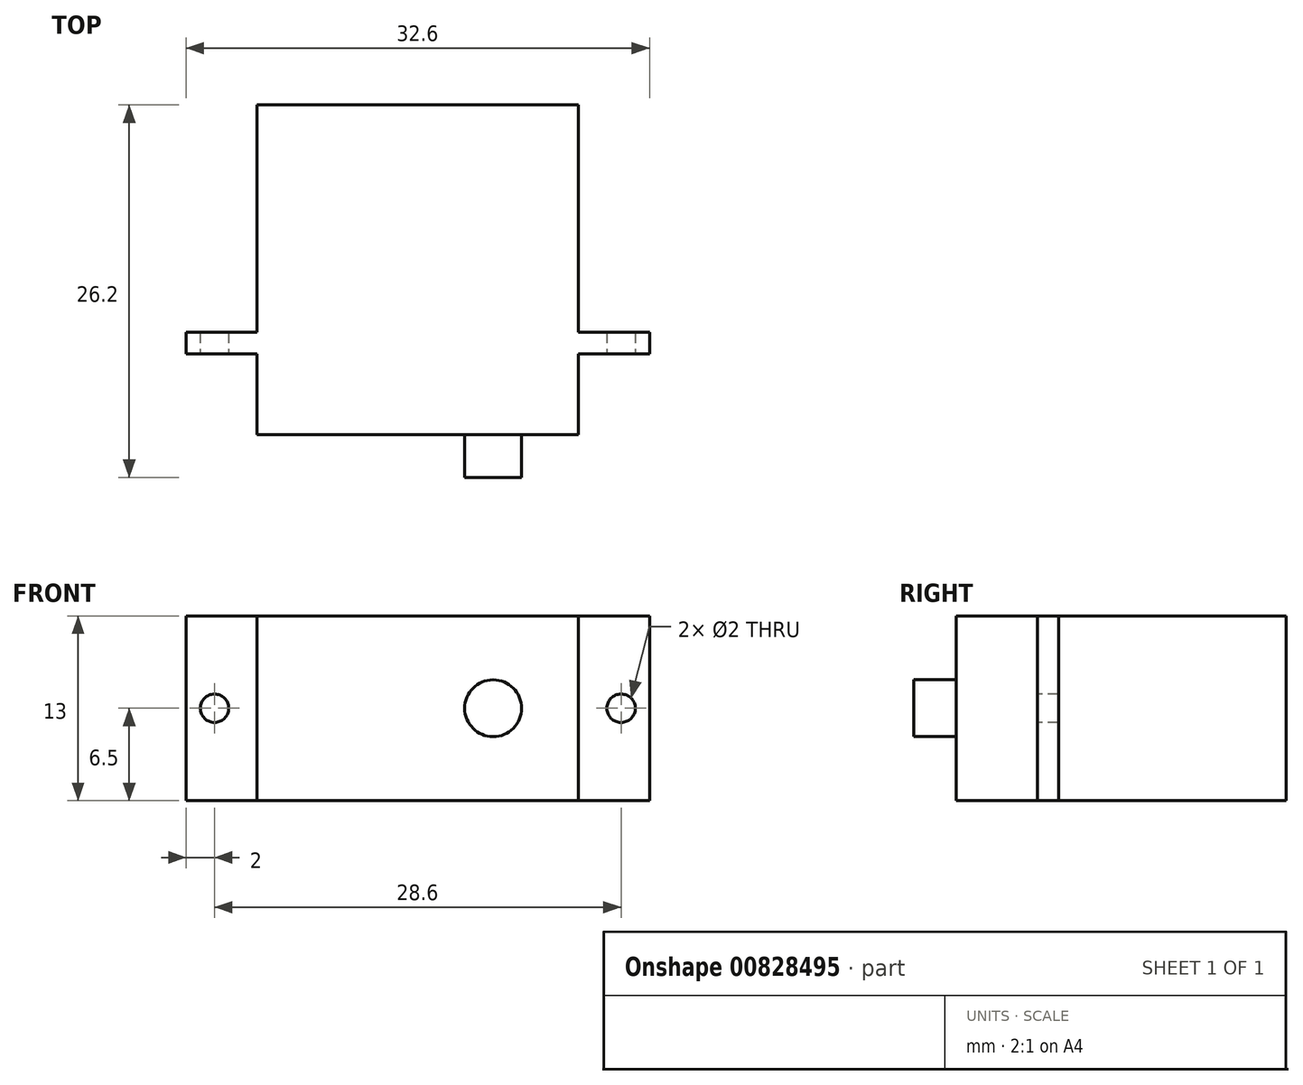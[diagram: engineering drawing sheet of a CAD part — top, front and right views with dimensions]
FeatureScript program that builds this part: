
annotation { "Feature Type Name" : "Feature", "Feature Type Description" : "" }
export const myFeature = defineFeature(function(context is Context, id is Id, definition is map)
    precondition{}
    {
        {
            var Q0;
            Q0=qCreatedBy(makeId("Top.planeOp"),FACE);
            var sketch = newSketch(context, id + "F0", { "sketchPlane" : qUnion([Q0])});
            skLineSegment(sketch, "E0", {"start": v(-33.3, 20.69) * mm, "end": v(-10.7, 20.69) * mm});
            skLineSegment(sketch, "E1", {"start": v(-10.7, 20.69) * mm, "end": v(-10.7, 4.69) * mm});
            skLineSegment(sketch, "E2", {"start": v(-10.7, 4.69) * mm, "end": v(-5.7, 4.69) * mm});
            skLineSegment(sketch, "E3", {"start": v(-5.7, 4.69) * mm, "end": v(-5.7, 3.19) * mm});
            skLineSegment(sketch, "E4", {"start": v(-5.7, 3.19) * mm, "end": v(-10.7, 3.19) * mm});
            skLineSegment(sketch, "E5", {"start": v(-10.7, 3.19) * mm, "end": v(-10.7, -2.51) * mm});
            skLineSegment(sketch, "E6", {"start": v(-10.7, -2.51) * mm, "end": v(-33.3, -2.51) * mm});
            skLineSegment(sketch, "E7", {"start": v(-33.3, -2.51) * mm, "end": v(-33.3, 3.19) * mm});
            skLineSegment(sketch, "E8", {"start": v(-33.3, 3.19) * mm, "end": v(-38.3, 3.19) * mm});
            skLineSegment(sketch, "E9", {"start": v(-38.3, 3.19) * mm, "end": v(-38.3, 4.69) * mm});
            skLineSegment(sketch, "E10", {"start": v(-38.3, 4.69) * mm, "end": v(-33.3, 4.69) * mm});
            skLineSegment(sketch, "E11", {"start": v(-33.3, 4.69) * mm, "end": v(-33.3, 20.69) * mm});
            skPoint(sketch, "E12", {"position": v(-16.7, -2.51) * mm});
            skPoint(sketch, "E13", {"position": v(-16.7, -8.17) * mm});
            skLineSegment(sketch, "E14", {"start": v(-16.7, -2.51) * mm, "end": v(-16.7, -8.17) * mm, "construction": true});
            skSolve(sketch);
        }
        {
            var Q0;
            Q0=makeQuery(id+"F0.imprint","IMPRINT",FACE,{"disambiguationData":[TD([[makeQuery(id+"F0.imprint","IMPRINT",EDGE,{"derivedFrom":sQuery(id+"F0.wireOp",EDGE,"E0")}),-1.0]])]});
            extrude(context, id + "F1", {"entities" : qUnion([Q0]), "depth" : 13 * mm, "offsetDistance" : 25 * mm});
        }
        {
            var Q0;
            Q0=makeQuery(id+"F1.opExtrude","SWEPT_FACE",FACE,{"disambiguationData":[OSD([sQuery(id+"F0.wireOp",EDGE,"E4")])]});
            var sketch = newSketch(context, id + "F2", { "sketchPlane" : qUnion([Q0])});
            skLineSegment(sketch, "E15.0.0", {"start": v(-38.3, 0) * mm, "end": v(-33.3, 0) * mm, "construction": true});
            skLineSegment(sketch, "E15.0.1", {"start": v(-33.3, 0) * mm, "end": v(-33.3, 13) * mm, "construction": true});
            skLineSegment(sketch, "E15.0.2", {"start": v(-33.3, 13) * mm, "end": v(-38.3, 13) * mm, "construction": true});
            skLineSegment(sketch, "E15.0.3", {"start": v(-38.3, 13) * mm, "end": v(-38.3, 0) * mm, "construction": true});
            skLineSegment(sketch, "E16.0", {"start": v(-5.7, 13) * mm, "end": v(-10.7, 13) * mm, "construction": true});
            skLineSegment(sketch, "E16.1", {"start": v(-5.7, 13) * mm, "end": v(-5.7, 0) * mm, "construction": true});
            skLineSegment(sketch, "E16.2", {"start": v(-10.7, 13) * mm, "end": v(-10.7, 0) * mm, "construction": true});
            skLineSegment(sketch, "E16.3", {"start": v(-5.7, 0) * mm, "end": v(-10.7, 0) * mm, "construction": true});
            skLineSegment(sketch, "E17", {"start": v(-5.7, 6.5) * mm, "end": v(-7.7, 6.5) * mm, "construction": true});
            skLineSegment(sketch, "E18", {"start": v(-38.3, 6.5) * mm, "end": v(-36.3, 6.5) * mm, "construction": true});
            skCircle(sketch, "E19", {"center": v(-36.3, 6.5) * mm, "radius": 1 * mm});
            skCircle(sketch, "E20", {"center": v(-7.7, 6.5) * mm, "radius": 1 * mm});
            skSolve(sketch);
        }
        {
            var Q0;
            Q0=makeQuery(id+"F2.imprint","IMPRINT",FACE,{"disambiguationData":[TD([[makeQuery(id+"F2.imprint","IMPRINT",EDGE,{"derivedFrom":sQuery(id+"F2.wireOp",EDGE,"E19")}),1.0]])]});
            var Q1;
            Q1=makeQuery(id+"F2.imprint","IMPRINT",FACE,{"disambiguationData":[TD([[makeQuery(id+"F2.imprint","IMPRINT",EDGE,{"derivedFrom":sQuery(id+"F2.wireOp",EDGE,"E20")}),1.0]])]});
            var Q2;
            Q2=makeQuery(id+"F1.opExtrude","SWEPT_FACE",FACE,{"disambiguationData":[OSD([sQuery(id+"F0.wireOp",EDGE,"E2")])]});
            extrude(context, id + "F3", {"entities" : qUnion([Q0, Q1]), "operationType" : NewBodyOperationType.REMOVE, "endBound" : BoundingType.UP_TO_SURFACE, "oppositeDirection" : true, "depth" : 25 * mm, "endBoundEntityFace" : qUnion([Q2]), "offsetDistance" : 25 * mm});
        }
        {
            var Q0;
            Q0=makeQuery(id+"F1.opExtrude","SWEPT_FACE",FACE,{"disambiguationData":[OSD([sQuery(id+"F0.wireOp",EDGE,"E6")])]});
            var sketch = newSketch(context, id + "F4", { "sketchPlane" : qUnion([Q0])});
            skLineSegment(sketch, "E21.0", {"start": v(-10.7, 13) * mm, "end": v(-10.7, 0) * mm, "construction": true});
            skLineSegment(sketch, "E22", {"start": v(-10.7, 6.5) * mm, "end": v(-16.7, 6.5) * mm, "construction": true});
            skCircle(sketch, "E23", {"center": v(-16.7, 6.5) * mm, "radius": 2 * mm});
            skSolve(sketch);
        }
        {
            var Q0;
            Q0=makeQuery(id+"F4.imprint","IMPRINT",FACE,{"disambiguationData":[TD([[makeQuery(id+"F4.imprint","IMPRINT",EDGE,{"derivedFrom":sQuery(id+"F4.wireOp",EDGE,"E23")}),1.0]])]});
            extrude(context, id + "F5", {"entities" : qUnion([Q0]), "operationType" : NewBodyOperationType.ADD, "depth" : 3 * mm, "offsetDistance" : 25 * mm});
        }
    });
